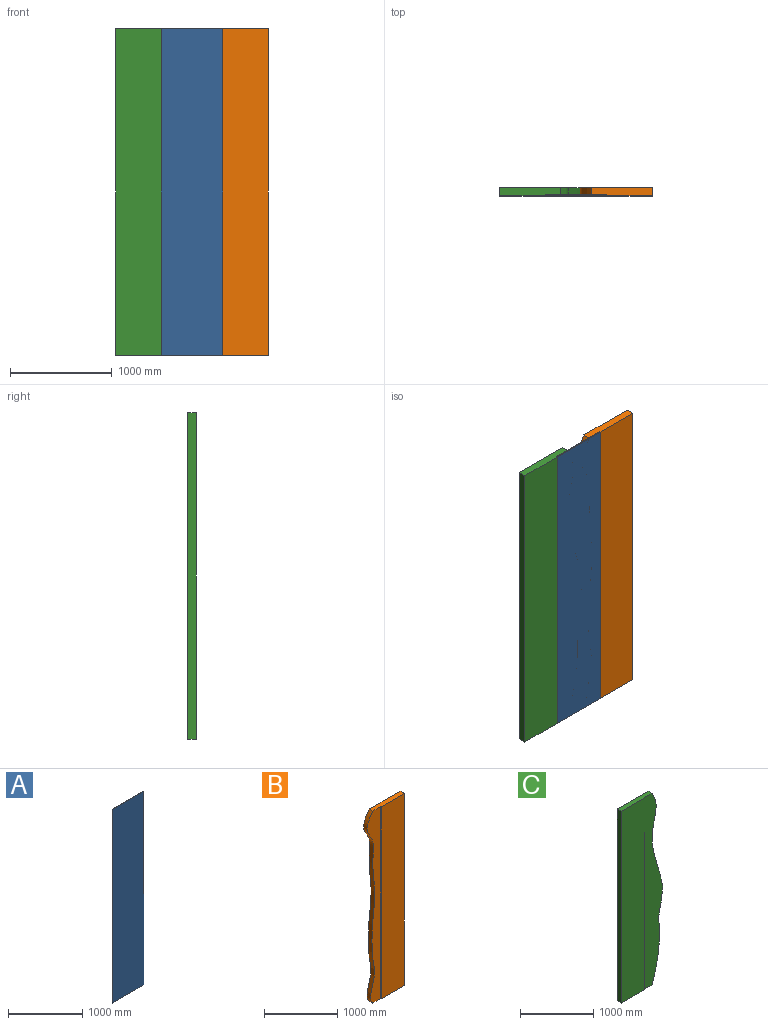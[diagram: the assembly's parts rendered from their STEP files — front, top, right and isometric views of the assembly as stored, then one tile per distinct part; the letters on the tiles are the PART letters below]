
ASSEMBLY  parts=3 mates=2
PART A: 6 faces, bbox 600x10x3200 mm
  f0: plane 3200x10mm, normal (-1,0,0), area 32000mm2, adj f1,f3,f4,f5
  f1: plane 600x10mm, normal (0,0,-1), area 6000mm2, adj f0,f2,f4,f5
  f2: plane 3200x10mm, normal (1,0,0), area 32000mm2, adj f1,f3,f4,f5
  f3: plane 600x10mm, normal (0,0,1), area 6000mm2, adj f0,f2,f4,f5
  f4: plane 3200x600mm, normal (0,-1,0), area 1920000mm2, adj f0,f1,f2,f3
  f5: plane 3200x600mm, normal (0,1,0), area 1920000mm2, adj f0,f1,f2,f3
PART B: 8 faces, bbox 727.2x80x3200 mm
  f0: extruded ~3200x146.5mm, area 229432.9mm2, adj f1,f3,f5,f7
  f1: plane 600x80mm, normal (0,0,-1), area 46500mm2, adj f0,f2,f4,f5,f6,f7
  f2: plane 3200x80mm, normal (1,0,0), area 256000mm2, adj f1,f3,f4,f5
  f3: plane 600x80mm, normal (0,0,1), area 46500mm2, adj f0,f2,f4,f5,f6,f7
  f4: plane 3200x450mm, normal (0,-1,0), area 1440000mm2, adj f1,f2,f3,f6
  f5: plane 3200x727.17mm, normal (0,1,0), area 1933320.9mm2, adj f0,f1,f2,f3
  f6: plane 3200x10mm, normal (-1,0,0), area 32000mm2, adj f1,f3,f4,f7
  f7: plane 3200x277.17mm, normal (0,-1,0), area 493320.9mm2, adj f0,f1,f3,f6
PART C: 8 faces, bbox 819.3x80x3200 mm
  f0: plane 600x80mm, normal (0,0,-1), area 46500mm2, adj f1,f3,f4,f5,f6,f7
  f1: extruded ~3200x199.54mm, area 228612.6mm2, adj f0,f2,f5,f7
  f2: plane 600x80mm, normal (0,0,1), area 46500mm2, adj f1,f3,f4,f5,f6,f7
  f3: plane 3200x450mm, normal (0,-1,0), area 1440000mm2, adj f0,f2,f4,f6
  f4: plane 3200x80mm, normal (-1,0,0), area 256000mm2, adj f0,f2,f3,f5
  f5: plane 3200x819.34mm, normal (0,1,0), area 2218553.8mm2, adj f0,f1,f2,f4
  f6: plane 3200x10mm, normal (1,0,0), area 32000mm2, adj f0,f2,f3,f7
  f7: plane 3200x369.34mm, normal (0,-1,0), area 778569.2mm2, adj f0,f1,f2,f6
PLACE A rot(axis=(0,0,1),180deg) t=(-1974.74,-244.33,-512.21)mm
PLACE B t=(-1224.74,-164.33,-512.21)mm fixed
PLACE C t=(-2724.74,-164.33,-512.21)mm
MATE planar A.f5 <-> B.f4  axis (0,-1,0) through (-1974.74,-244.33,2687.79)mm
MATE planar B.f4 <-> C.f3  axis (0,-1,0) through (-1224.74,-244.33,1087.79)mm
